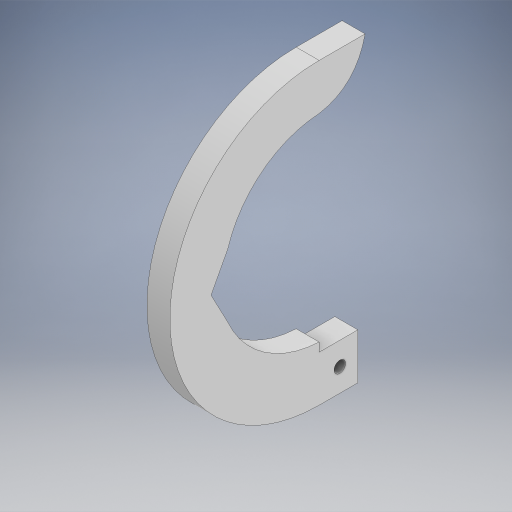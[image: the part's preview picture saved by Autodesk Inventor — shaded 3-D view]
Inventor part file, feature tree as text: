
AUTODESK INVENTOR PART (.ipt)
format: ipt  version: 2024.2 (Build 282272000, 272)  size: 281,088 bytes
history: native  units: in
note: dims shown in document units (in); Inventor stores cm internally (conversion verified against a paired STEP export)
features: extrude x1, sketch x1
ambient origin geometry x8: Origin, YZ Plane, XZ Plane, XY Plane, X Axis, Y Axis, Z Axis, Center Point
bodies: Body1 (feature_tree)
feature tree (2):
  extrude  "Extrusion2"  Depth=0.5in TaperAngle=0.0deg
  sketch  "Sketch1"  dims[d0=4.5in d1=2.25in d2=1.0in d5=0.5in d6=0.0in d7=0.5in d8=0.0344in]
